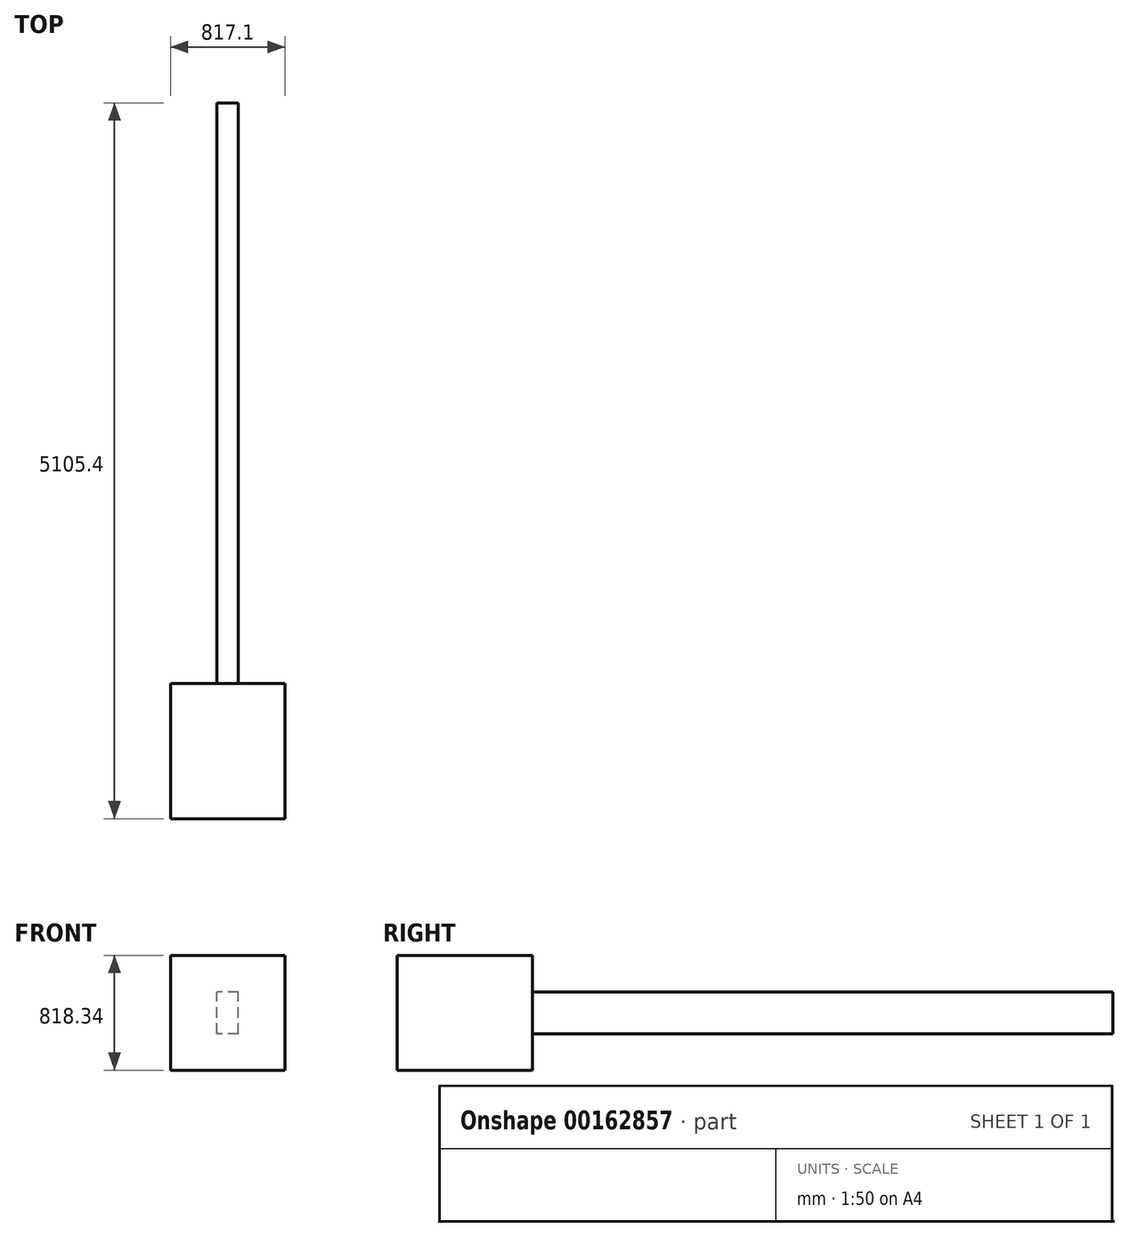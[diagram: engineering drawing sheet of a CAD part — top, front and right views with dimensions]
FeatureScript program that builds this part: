
annotation { "Feature Type Name" : "Feature", "Feature Type Description" : "" }
export const myFeature = defineFeature(function(context is Context, id is Id, definition is map)
    precondition{}
    {
        {
            var Q0;
            Q0=qCreatedBy(makeId("Front.planeOp"),FACE);
            var sketch = newSketch(context, id + "F0", { "sketchPlane" : qUnion([Q0])});
            skLineSegment(sketch, "E0.bottom", {"start": v(76.2, -149.23) * mm, "end": v(-76.2, -149.23) * mm});
            skLineSegment(sketch, "E0.top", {"start": v(76.2, 149.23) * mm, "end": v(-76.2, 149.23) * mm});
            skLineSegment(sketch, "E0.left", {"start": v(76.2, -149.23) * mm, "end": v(76.2, 149.22) * mm});
            skLineSegment(sketch, "E0.right", {"start": v(-76.2, -149.23) * mm, "end": v(-76.2, 149.22) * mm});
            skPoint(sketch, "E0.middle", {"position": v(0, 0) * mm});
            skSolve(sketch);
        }
        {
            var Q0;
            Q0=makeQuery(id+"F0.imprint","IMPRINT",FACE,{"disambiguationData":[TD([[makeQuery(id+"F0.imprint","IMPRINT",EDGE,{"derivedFrom":sQuery(id+"F0.wireOp",EDGE,"E0.bottom")}),-1.0]])]});
            extrude(context, id + "F1", {"entities" : qUnion([Q0]), "depth" : 4140.2 * mm});
        }
        {
            var Q0;
            Q0=makeQuery(id+"F1.opExtrude","CAP_FACE",FACE,{"disambiguationData":[OSD([sQuery(id+"F0.wireOp",EDGE,"E0.bottom"),sQuery(id+"F0.wireOp",EDGE,"E0.top"),sQuery(id+"F0.wireOp",EDGE,"E0.left"),sQuery(id+"F0.wireOp",EDGE,"E0.right")])],"isStart":false});
            var sketch = newSketch(context, id + "F2", { "sketchPlane" : qUnion([Q0])});
            skLineSegment(sketch, "E1.bottom", {"start": v(408.55, -409.17) * mm, "end": v(-408.55, -409.17) * mm});
            skLineSegment(sketch, "E1.top", {"start": v(408.55, 409.17) * mm, "end": v(-408.55, 409.17) * mm});
            skLineSegment(sketch, "E1.left", {"start": v(408.55, -409.17) * mm, "end": v(408.55, 409.17) * mm});
            skLineSegment(sketch, "E1.right", {"start": v(-408.55, -409.17) * mm, "end": v(-408.55, 409.17) * mm});
            skPoint(sketch, "E1.middle", {"position": v(0, 0) * mm});
            skSolve(sketch);
        }
        {
            var Q0;
            Q0 = qSketchRegion(id + "F2", true);
            extrude(context, id + "F3", {"entities" : qUnion([Q0]), "operationType" : NewBodyOperationType.ADD, "depth" : 965.2 * mm});
        }
    });
